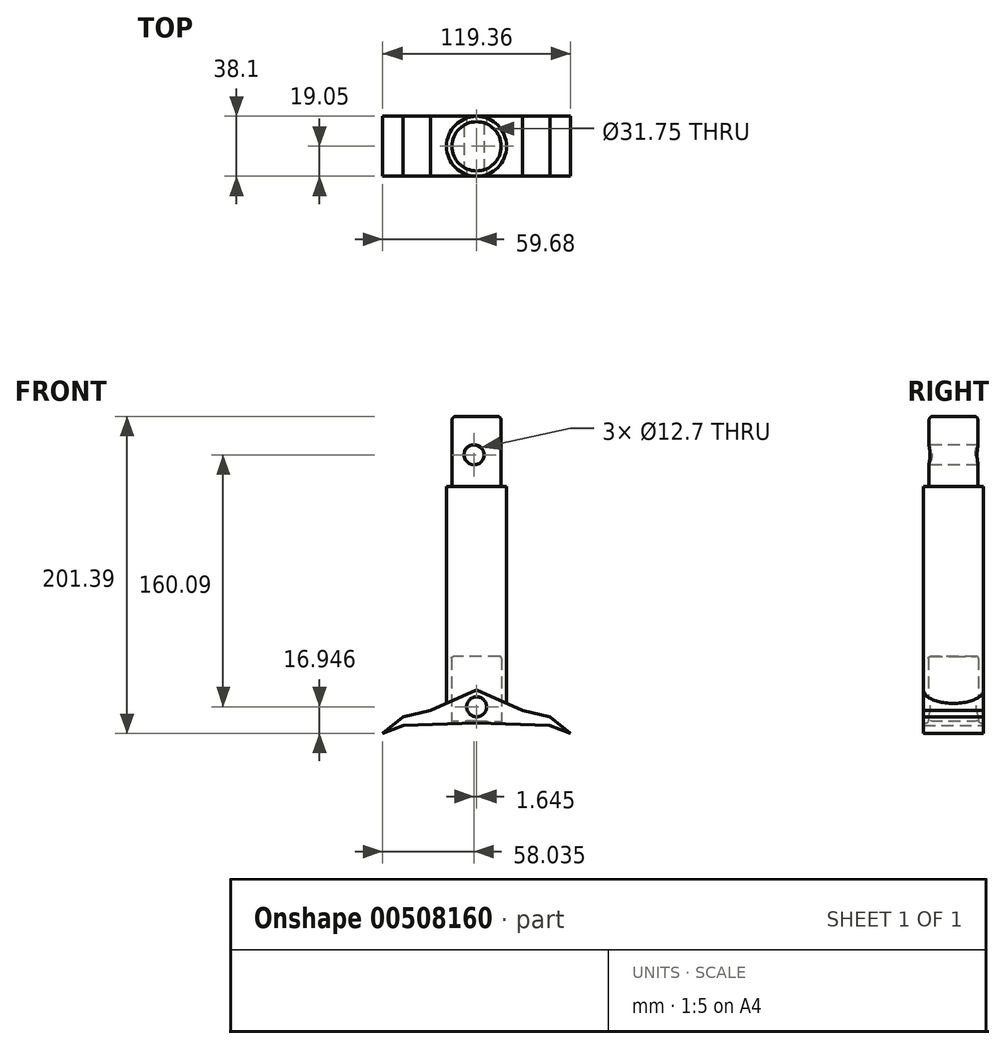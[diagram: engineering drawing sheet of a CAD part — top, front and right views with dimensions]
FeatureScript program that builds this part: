
annotation { "Feature Type Name" : "Feature", "Feature Type Description" : "" }
export const myFeature = defineFeature(function(context is Context, id is Id, definition is map)
    precondition{}
    {
        {
            var Q0;
            Q0=qCreatedBy(makeId("Top.planeOp"),FACE);
            var sketch = newSketch(context, id + "F0", { "sketchPlane" : qUnion([Q0])});
            skCircle(sketch, "E0", {"center": v(0, 0) * mm, "radius": 15.62 * mm});
            skSolve(sketch);
        }
        {
            var Q0;
            Q0 = qSketchRegion(id + "F0", true);
            extrude(context, id + "F1", {"entities" : qUnion([Q0]), "depth" : 44.45 * mm});
        }
        {
            var Q0;
            Q0=qCreatedBy(makeId("Front.planeOp"),FACE);
            var sketch = newSketch(context, id + "F2", { "sketchPlane" : qUnion([Q0])});
            skCircle(sketch, "E1", {"center": v(-1.64, 20.1) * mm, "radius": 6.35 * mm});
            skPoint(sketch, "E2.center.orphan", {"position": v(0, 20.1) * mm});
            skSolve(sketch);
        }
        {
            var Q0;
            Q0 = qSketchRegion(id + "F2", true);
            extrude(context, id + "F3", {"entities" : qUnion([Q0]), "operationType" : NewBodyOperationType.REMOVE, "oppositeDirection" : true, "depth" : 49.28 * mm, "symmetric" : true});
        }
        {
            var Q0;
            Q0=qCreatedBy(makeId("Top.planeOp"),FACE);
            var sketch = newSketch(context, id + "F4", { "sketchPlane" : qUnion([Q0]), "disableImprinting" : false});
            skEllipse(sketch, "E3", {"center": v(0, 0) * mm, "majorRadius": 19.05 * mm, "minorRadius": 19.05 * mm, "majorAxis": v(1, 0)});
            skSolve(sketch);
        }
        {
            var Q0;
            Q0=makeQuery(id+"F4.imprint","IMPRINT",FACE,{"disambiguationData":[TD([[makeQuery(id+"F4.imprint","IMPRINT",EDGE,{"derivedFrom":sQuery(id+"F4.wireOp",EDGE,"E3")}),1.0]])]});
            extrude(context, id + "F5", {"entities" : qUnion([Q0]), "operationType" : NewBodyOperationType.ADD, "oppositeDirection" : true, "depth" : 149.86 * mm});
        }
        {
            var Q0;
            Q0=qCreatedBy(makeId("Front.planeOp"),FACE);
            var sketch = newSketch(context, id + "F6", { "sketchPlane" : qUnion([Q0])});
            skPoint(sketch, "E4.orphan", {"position": v(0, -150.15) * mm});
            skLineSegment(sketch, "E5", {"start": v(0, -129.34) * mm, "end": v(29.13, -142.38) * mm});
            skLineSegment(sketch, "E6", {"start": v(0, -150.15) * mm, "end": v(46.33, -151.67) * mm});
            skLineSegment(sketch, "E7", {"start": v(46.33, -151.67) * mm, "end": v(59.68, -156.94) * mm});
            skLineSegment(sketch, "E8", {"start": v(59.68, -156.94) * mm, "end": v(46.7, -146.56) * mm});
            skLineSegment(sketch, "E9", {"start": v(46.7, -146.56) * mm, "end": v(32.66, -143.22) * mm});
            skLineSegment(sketch, "E10", {"start": v(29.13, -142.38) * mm, "end": v(0, -129.34) * mm});
            skPoint(sketch, "E11.MirrorP", {"position": v(-0.61, -150.15) * mm});
            skLineSegment(sketch, "E12", {"start": v(32.66, -143.22) * mm, "end": v(29.13, -142.38) * mm});
            skLineSegment(sketch, "E13", {"start": v(0, -129.34) * mm, "end": v(0, -150.15) * mm, "construction": true});
            skLineSegment(sketch, "E14.MirrorCS", {"start": v(-32.66, -143.22) * mm, "end": v(-29.13, -142.38) * mm});
            skLineSegment(sketch, "E15.MirrorCS", {"start": v(0, -129.34) * mm, "end": v(-29.13, -142.38) * mm});
            skLineSegment(sketch, "E16.MirrorCS", {"start": v(-46.33, -151.67) * mm, "end": v(-59.68, -156.94) * mm});
            skLineSegment(sketch, "E17.MirrorCS", {"start": v(-46.7, -146.56) * mm, "end": v(-32.66, -143.22) * mm});
            skLineSegment(sketch, "E18.MirrorCS", {"start": v(-59.68, -156.94) * mm, "end": v(-46.7, -146.56) * mm});
            skLineSegment(sketch, "E19.MirrorCS", {"start": v(0, -150.15) * mm, "end": v(-46.33, -151.67) * mm});
            skLineSegment(sketch, "E20.MirrorCS", {"start": v(-29.13, -142.38) * mm, "end": v(0, -129.34) * mm});
            skLineSegment(sketch, "E21", {"start": v(-59.68, -156.94) * mm, "end": v(59.68, -156.94) * mm, "construction": true});
            skLineSegment(sketch, "E22", {"start": v(0, -156.94) * mm, "end": v(0, 44.67) * mm, "construction": true});
            skSolve(sketch);
        }
        {
            var Q0;
            Q0=makeQuery(id+"F6.imprint","IMPRINT",FACE,{"disambiguationData":[TD([[makeQuery(id+"F6.imprint","IMPRINT",EDGE,{"derivedFrom":sQuery(id+"F6.wireOp",EDGE,"E6")}),1.0]])]});
            extrude(context, id + "F7", {"entities" : qUnion([Q0]), "operationType" : NewBodyOperationType.ADD, "depth" : 38.1 * mm, "symmetric" : true});
        }
        {
            var Q0;
            Q0=qCreatedBy(makeId("Top.planeOp"),FACE);
            cPlane(context, id + "F8", {"entities" : qUnion([Q0]), "cplaneType" : CPlaneType.OFFSET, "offset" : 152.4 * mm, "oppositeDirection" : true, "width" : 152.4 * mm, "height" : 152.4 * mm});
        }
        {
            var Q0;
            Q0=qCreatedBy(id+"F8.planeOp",FACE);
            var sketch = newSketch(context, id + "F9", { "sketchPlane" : qUnion([Q0])});
            skCircle(sketch, "E23", {"center": v(0, 0) * mm, "radius": 15.88 * mm});
            skSolve(sketch);
        }
        {
            var Q0;
            Q0 = qSketchRegion(id + "F9", true);
            extrude(context, id + "F10", {"entities" : qUnion([Q0]), "operationType" : NewBodyOperationType.REMOVE, "depth" : 44.45 * mm});
        }
        {
            var Q0;
            Q0=qCreatedBy(makeId("Front.planeOp"),FACE);
            var sketch = newSketch(context, id + "F11", { "sketchPlane" : qUnion([Q0])});
            skCircle(sketch, "E24", {"center": v(0, -140) * mm, "radius": 6.35 * mm});
            skSolve(sketch);
        }
        {
            var Q0;
            Q0=makeQuery(id+"F11.imprint","IMPRINT",FACE,{"disambiguationData":[TD([[makeQuery(id+"F11.imprint","IMPRINT",EDGE,{"derivedFrom":sQuery(id+"F11.wireOp",EDGE,"E24")}),1.0]])]});
            var Q1;
            Q1=sQuery(id+"F11.wireOp",EDGE,"E24");
            extrude(context, id + "F12", {"entities" : qUnion([Q0]), "operationType" : NewBodyOperationType.REMOVE, "surfaceEntities" : qUnion([Q1]), "oppositeDirection" : true, "depth" : 110.02 * mm, "symmetric" : true});
        }
        {
            var Q0;
            Q0=makeQuery(id+"F1.opExtrude","CAP_EDGE",EDGE,{"disambiguationData":[OSD([sQuery(id+"F0.wireOp",EDGE,"E0")])],"isStart":false});
            var Q1;
            Q1=makeQuery(id+"F1.opExtrude","CAP_EDGE",EDGE,{"disambiguationData":[OSD([sQuery(id+"F0.wireOp",EDGE,"E0")])],"isStart":true});
            fillet(context, id + "F13", {"entities" : qUnion([Q0, Q1]), "radius" : 2.54 * mm, "tangentPropagation" : true, "allowEdgeOverflow" : false});
        }
        {
            var Q0;
            Q0=makeQuery(id+"F10.boolean.opBoolean","COPY",EDGE,{"derivedFrom":makeQuery(id+"F10.opExtrude","CAP_EDGE",EDGE,{"disambiguationData":[OSD([sQuery(id+"F9.wireOp",EDGE,"E23")])],"isStart":false})});
            var Q1;
            Q1=makeQuery(id+"F10.boolean.opBoolean","INTERSECT",EDGE,{"derivedFrom":[makeQuery(id+"F7.opExtrude","SWEPT_FACE",FACE,{"disambiguationData":[OSD([sQuery(id+"F6.wireOp",EDGE,"E6")])]}),makeQuery(id+"F10.opExtrude","SWEPT_FACE",FACE,{"disambiguationData":[OSD([sQuery(id+"F9.wireOp",EDGE,"E23")])]})]});
            var Q2;
            Q2=makeQuery(id+"F10.boolean.opBoolean","INTERSECT",EDGE,{"derivedFrom":[makeQuery(id+"F7.opExtrude","SWEPT_FACE",FACE,{"disambiguationData":[OSD([sQuery(id+"F6.wireOp",EDGE,"E19.MirrorCS")])]}),makeQuery(id+"F10.opExtrude","SWEPT_FACE",FACE,{"disambiguationData":[OSD([sQuery(id+"F9.wireOp",EDGE,"E23")])]})]});
            fillet(context, id + "F14", {"entities" : qUnion([Q0, Q1, Q2]), "radius" : 1.27 * mm, "tangentPropagation" : true, "allowEdgeOverflow" : false});
        }
    });
